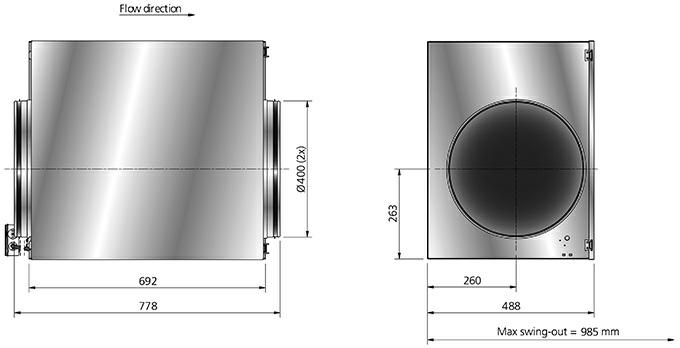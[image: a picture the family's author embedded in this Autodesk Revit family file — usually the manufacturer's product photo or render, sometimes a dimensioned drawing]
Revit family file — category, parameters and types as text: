
# Revit family: IRE 630 D3 ErP AC
name_source: partatom
category: Mechanical Equipment
revit_build: Autodesk Revit MEP 2014 (Build: 20130308_1515(x64)
units: mm (PartAtom-declared; Revit-internal decimal feet)

## types (1)
- IRE 630 D3 ErP AC
    Capacitor = - μF
    Current = 7 A
    Depth = 955 mm  [stored 3.1332 ft]
    Description = Insulated duct fans with circular connections
    Diameter = 630 mm  [stored 2.06693 ft]
    Frequency = 50 Hz
    Height = 703 mm  [stored 2.30643 ft]
    Main Material = Steel, Galvanized
    Max. temperature of transported air = 60 °C
    Max. temperature of transported air when speed controlled = 50 °C
    Phase = 3
    Power = 4000 W
    Sound pressure level at 3 m = 51 dB(A)
    Speed = 870 rpm
    Voltage = 400 V
    Voltage range = 380-415 V
    Weight = 115.00 kg
    Width = 1067 mm  [stored 3.50066 ft]
    Wiring diagram = Y 4040004 / Δ 4040003

note: [stored X ft] marks values corroborated as IEEE doubles in the binary element streams (Revit-internal decimal feet)

## geometry (parser evidence)
native form markers: Sweep x5
no freeform markers — native parametric forms only
